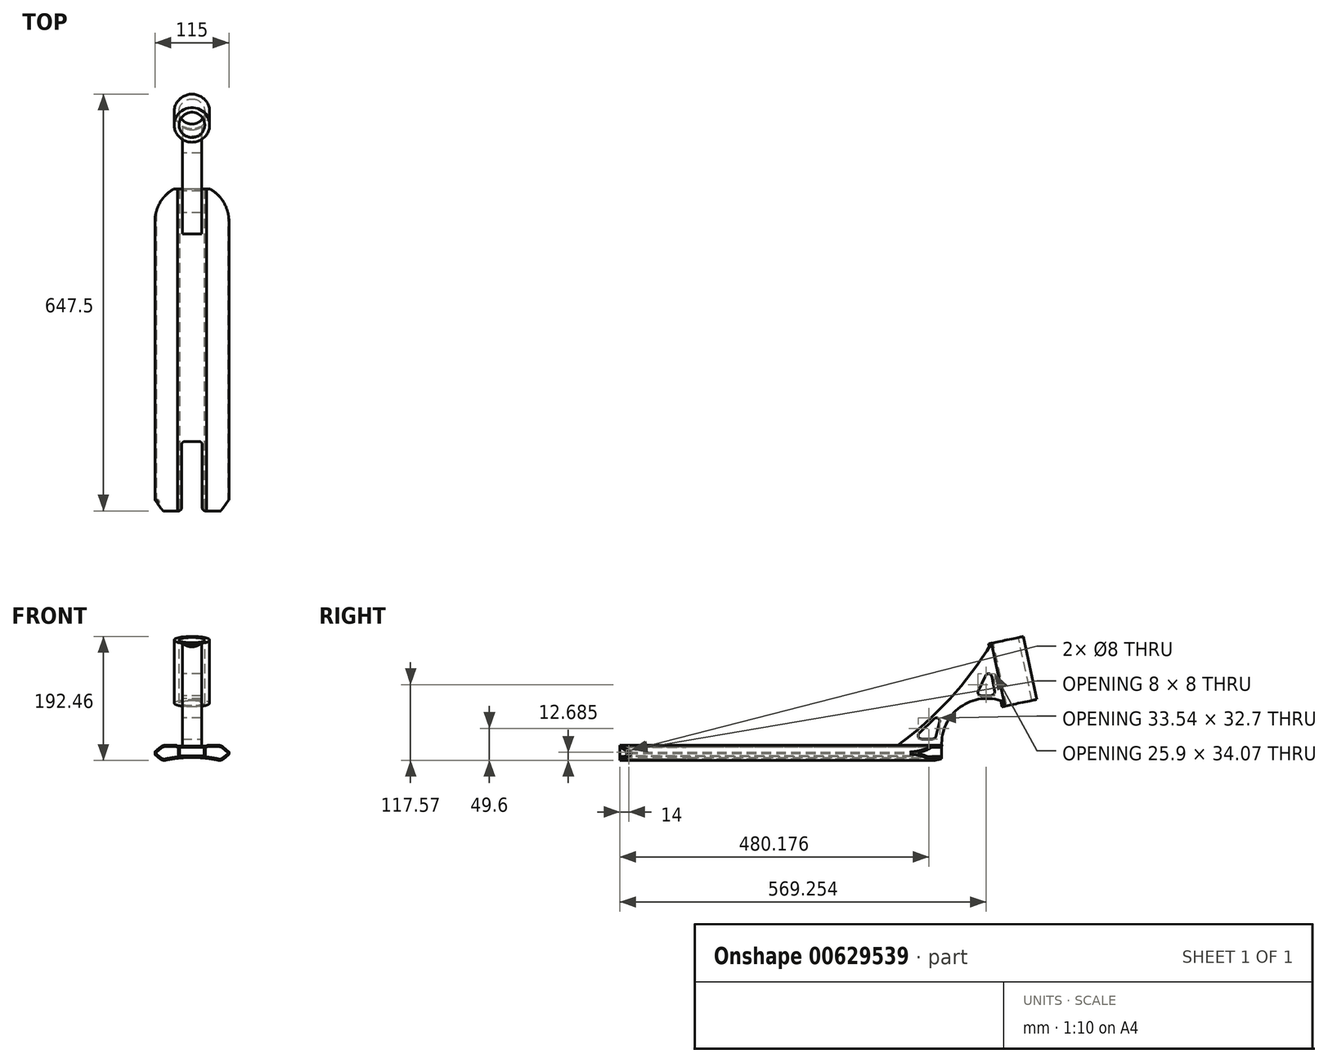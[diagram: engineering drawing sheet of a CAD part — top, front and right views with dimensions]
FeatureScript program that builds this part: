
annotation { "Feature Type Name" : "Feature", "Feature Type Description" : "" }
export const myFeature = defineFeature(function(context is Context, id is Id, definition is map)
    precondition{}
    {
        {
            var Q0;
            Q0=qCreatedBy(makeId("Front.planeOp"),FACE);
            var sketch = newSketch(context, id + "F0", { "sketchPlane" : qUnion([Q0])});
            skLineSegment(sketch, "E0", {"start": v(0, 0) * mm, "end": v(0, 44.87) * mm, "construction": true});
            skLineSegment(sketch, "E1", {"start": v(0, 0) * mm, "end": v(22.5, 0) * mm});
            skLineSegment(sketch, "E2", {"start": v(22.5, 0) * mm, "end": v(22.5, 1.3) * mm});
            skLineSegment(sketch, "E3", {"start": v(22.5, 1.3) * mm, "end": v(45.58, 1.3) * mm});
            skLineSegment(sketch, "E4", {"start": v(45.58, 1.3) * mm, "end": v(57.5, -8.7) * mm});
            skLineSegment(sketch, "E5", {"start": v(57.5, -8.7) * mm, "end": v(57.5, -12.7) * mm});
            skLineSegment(sketch, "E6", {"start": v(57.5, -12.7) * mm, "end": v(45.58, -22.7) * mm});
            skLineSegment(sketch, "E7.MirrorCS", {"start": v(0, 0) * mm, "end": v(-22.5, 0) * mm});
            skLineSegment(sketch, "E8.MirrorCS", {"start": v(-22.5, 0) * mm, "end": v(-22.5, 1.3) * mm});
            skLineSegment(sketch, "E9.MirrorCS", {"start": v(-22.5, 1.3) * mm, "end": v(-45.58, 1.3) * mm});
            skLineSegment(sketch, "E10.MirrorCS", {"start": v(-45.58, 1.3) * mm, "end": v(-57.5, -8.7) * mm});
            skLineSegment(sketch, "E11.MirrorCS", {"start": v(-57.5, -8.7) * mm, "end": v(-57.5, -12.7) * mm});
            skLineSegment(sketch, "E12.MirrorCS", {"start": v(-57.5, -12.7) * mm, "end": v(-45.58, -22.7) * mm});
            skArc(sketch, "E13", {"start": v(45.58, -22.7) * mm, "mid": v(0, -17.44) * mm, "end": v(-45.58, -22.7) * mm});
            skLineSegment(sketch, "E14", {"start": v(-45.58, 1.3) * mm, "end": v(-80.6, 1.3) * mm, "construction": true});
            skLineSegment(sketch, "E15", {"start": v(-57.5, -12.7) * mm, "end": v(-57.5, -34.53) * mm, "construction": true});
            skSolve(sketch);
        }
        {
            var Q0;
            Q0 = qSketchRegion(id + "F0", true);
            extrude(context, id + "F1", {"entities" : qUnion([Q0]), "endBound" : BoundingType.SYMMETRIC, "depth" : 500 * mm, "offsetDistance" : 25 * mm});
        }
        {
            var Q0;
            Q0=makeQuery(id+"F1.opExtrude","CAP_FACE",FACE,{"disambiguationData":[OSD([sQuery(id+"F0.wireOp",EDGE,"E1"),sQuery(id+"F0.wireOp",EDGE,"E2"),sQuery(id+"F0.wireOp",EDGE,"E3"),sQuery(id+"F0.wireOp",EDGE,"E4"),sQuery(id+"F0.wireOp",EDGE,"E5"),sQuery(id+"F0.wireOp",EDGE,"E6"),sQuery(id+"F0.wireOp",EDGE,"E7.MirrorCS"),sQuery(id+"F0.wireOp",EDGE,"E8.MirrorCS"),sQuery(id+"F0.wireOp",EDGE,"E9.MirrorCS"),sQuery(id+"F0.wireOp",EDGE,"E10.MirrorCS"),sQuery(id+"F0.wireOp",EDGE,"E11.MirrorCS"),sQuery(id+"F0.wireOp",EDGE,"E12.MirrorCS"),sQuery(id+"F0.wireOp",EDGE,"E13")])],"isStart":false});
            var sketch = newSketch(context, id + "F2", { "sketchPlane" : qUnion([Q0])});
            skLineSegment(sketch, "E16.bottom", {"start": v(-19, -2) * mm, "end": v(19, -2) * mm});
            skLineSegment(sketch, "E16.top", {"start": v(-19, -15) * mm, "end": v(19, -15) * mm});
            skLineSegment(sketch, "E16.left", {"start": v(-19, -2) * mm, "end": v(-19, -15) * mm});
            skLineSegment(sketch, "E16.right", {"start": v(19, -2) * mm, "end": v(19, -15) * mm});
            skSolve(sketch);
        }
        {
            var Q0;
            Q0 = qSketchRegion(id + "F2", true);
            extrude(context, id + "F3", {"entities" : qUnion([Q0]), "operationType" : NewBodyOperationType.REMOVE, "endBound" : BoundingType.THROUGH_ALL, "oppositeDirection" : true, "depth" : 1068 * mm, "offsetDistance" : 25 * mm});
        }
        {
            var Q0;
            Q0=makeQuery(id+"F1.opExtrude","SWEPT_EDGE",EDGE,{"disambiguationData":[OSD([sQuery(id+"F0.wireOp",EDGE,"E8.MirrorCS"),sQuery(id+"F0.wireOp",EDGE,"E9.MirrorCS")])]});
            var Q1;
            Q1=makeQuery(id+"F1.opExtrude","SWEPT_EDGE",EDGE,{"disambiguationData":[OSD([sQuery(id+"F0.wireOp",EDGE,"E2"),sQuery(id+"F0.wireOp",EDGE,"E3")])]});
            fillet(context, id + "F4", {"entities" : qUnion([Q0, Q1]), "radius" : 2 * mm, "tangentPropagation" : true, "allowEdgeOverflow" : false});
        }
        {
            var Q0;
            Q0=makeQuery(id+"F1.opExtrude","SWEPT_EDGE",EDGE,{"disambiguationData":[OSD([sQuery(id+"F0.wireOp",EDGE,"E9.MirrorCS"),sQuery(id+"F0.wireOp",EDGE,"E10.MirrorCS")])]});
            var Q1;
            Q1=makeQuery(id+"F1.opExtrude","SWEPT_EDGE",EDGE,{"disambiguationData":[OSD([sQuery(id+"F0.wireOp",EDGE,"E3"),sQuery(id+"F0.wireOp",EDGE,"E4")])]});
            var Q2;
            Q2=makeQuery(id+"F1.opExtrude","SWEPT_EDGE",EDGE,{"disambiguationData":[OSD([sQuery(id+"F0.wireOp",EDGE,"E6"),sQuery(id+"F0.wireOp",EDGE,"E13")])]});
            var Q3;
            Q3=makeQuery(id+"F1.opExtrude","SWEPT_EDGE",EDGE,{"disambiguationData":[OSD([sQuery(id+"F0.wireOp",EDGE,"E12.MirrorCS"),sQuery(id+"F0.wireOp",EDGE,"E13")])]});
            fillet(context, id + "F5", {"entities" : qUnion([Q0, Q1, Q2, Q3]), "radius" : 9 * mm, "tangentPropagation" : true, "allowEdgeOverflow" : false});
        }
        {
            var Q0;
            Q0=makeQuery(id+"F1.opExtrude","SWEPT_EDGE",EDGE,{"disambiguationData":[OSD([sQuery(id+"F0.wireOp",EDGE,"E4"),sQuery(id+"F0.wireOp",EDGE,"E5")])]});
            var Q1;
            Q1=makeQuery(id+"F1.opExtrude","SWEPT_EDGE",EDGE,{"disambiguationData":[OSD([sQuery(id+"F0.wireOp",EDGE,"E5"),sQuery(id+"F0.wireOp",EDGE,"E6")])]});
            var Q2;
            Q2=makeQuery(id+"F1.opExtrude","SWEPT_EDGE",EDGE,{"disambiguationData":[OSD([sQuery(id+"F0.wireOp",EDGE,"E10.MirrorCS"),sQuery(id+"F0.wireOp",EDGE,"E11.MirrorCS")])]});
            var Q3;
            Q3=makeQuery(id+"F1.opExtrude","SWEPT_EDGE",EDGE,{"disambiguationData":[OSD([sQuery(id+"F0.wireOp",EDGE,"E11.MirrorCS"),sQuery(id+"F0.wireOp",EDGE,"E12.MirrorCS")])]});
            fillet(context, id + "F6", {"entities" : qUnion([Q0, Q1, Q2, Q3]), "radius" : 1 * mm, "tangentPropagation" : true, "allowEdgeOverflow" : false});
        }
        {
            var Q0;
            Q0=makeQuery(id+"F1.opExtrude","CAP_FACE",FACE,{"disambiguationData":[OSD([sQuery(id+"F0.wireOp",EDGE,"E1"),sQuery(id+"F0.wireOp",EDGE,"E2"),sQuery(id+"F0.wireOp",EDGE,"E3"),sQuery(id+"F0.wireOp",EDGE,"E4"),sQuery(id+"F0.wireOp",EDGE,"E5"),sQuery(id+"F0.wireOp",EDGE,"E6"),sQuery(id+"F0.wireOp",EDGE,"E7.MirrorCS"),sQuery(id+"F0.wireOp",EDGE,"E8.MirrorCS"),sQuery(id+"F0.wireOp",EDGE,"E9.MirrorCS"),sQuery(id+"F0.wireOp",EDGE,"E10.MirrorCS"),sQuery(id+"F0.wireOp",EDGE,"E11.MirrorCS"),sQuery(id+"F0.wireOp",EDGE,"E12.MirrorCS"),sQuery(id+"F0.wireOp",EDGE,"E13")])],"isStart":false});
            var sketch = newSketch(context, id + "F7", { "sketchPlane" : qUnion([Q0])});
            skArc(sketch, "E17.0", {"start": v(-21, -16.53) * mm, "mid": v(-31.42, -17.9) * mm, "end": v(-41.75, -19.8) * mm});
            skArc(sketch, "E17.1", {"start": v(-47.7, -18.31) * mm, "mid": v(-44.9, -19.74) * mm, "end": v(-41.75, -19.8) * mm});
            skLineSegment(sketch, "E17.2", {"start": v(-55.5, -11.77) * mm, "end": v(-47.7, -18.31) * mm});
            skLineSegment(sketch, "E17.3", {"start": v(-55.5, -9.63) * mm, "end": v(-55.5, -11.77) * mm});
            skLineSegment(sketch, "E17.4", {"start": v(-24.37, -0.7) * mm, "end": v(-24.37, -0.7) * mm});
            skLineSegment(sketch, "E17.5", {"start": v(-24.37, -0.7) * mm, "end": v(-42.3, -0.7) * mm});
            skArc(sketch, "E17.6", {"start": v(-42.3, -0.7) * mm, "mid": v(-44.7, -1.12) * mm, "end": v(-46.8, -2.34) * mm});
            skLineSegment(sketch, "E17.7", {"start": v(-46.8, -2.34) * mm, "end": v(-55.5, -9.63) * mm});
            skLineSegment(sketch, "E18", {"start": v(-21, -16.53) * mm, "end": v(-21, -2) * mm});
            skLineSegment(sketch, "E19", {"start": v(-21, -2) * mm, "end": v(-22.88, -2) * mm});
            skArc(sketch, "E20", {"start": v(-22.88, -2) * mm, "mid": v(-23.38, -1.07) * mm, "end": v(-24.37, -0.7) * mm});
            skLineSegment(sketch, "E21.MirrorCS", {"start": v(21, -16.53) * mm, "end": v(21, -2) * mm});
            skLineSegment(sketch, "E22.MirrorCS", {"start": v(21, -2) * mm, "end": v(22.88, -2) * mm});
            skArc(sketch, "E23.MirrorCS", {"start": v(22.88, -2) * mm, "mid": v(23.38, -1.07) * mm, "end": v(24.37, -0.7) * mm});
            skLineSegment(sketch, "E24.MirrorCS", {"start": v(24.37, -0.7) * mm, "end": v(42.3, -0.7) * mm});
            skArc(sketch, "E25.MirrorCS", {"start": v(42.3, -0.7) * mm, "mid": v(44.7, -1.12) * mm, "end": v(46.8, -2.34) * mm});
            skLineSegment(sketch, "E26.MirrorCS", {"start": v(46.8, -2.34) * mm, "end": v(55.5, -9.63) * mm});
            skLineSegment(sketch, "E27.MirrorCS", {"start": v(55.5, -9.63) * mm, "end": v(55.5, -11.77) * mm});
            skLineSegment(sketch, "E28.MirrorCS", {"start": v(55.5, -11.77) * mm, "end": v(47.7, -18.31) * mm});
            skArc(sketch, "E29.MirrorCS", {"start": v(47.7, -18.31) * mm, "mid": v(44.9, -19.74) * mm, "end": v(41.75, -19.8) * mm});
            skArc(sketch, "E30.MirrorCS", {"start": v(21, -16.53) * mm, "mid": v(31.42, -17.9) * mm, "end": v(41.75, -19.8) * mm});
            skSolve(sketch);
        }
        {
            var Q0;
            Q0 = qSketchRegion(id + "F7", true);
            extrude(context, id + "F8", {"entities" : qUnion([Q0]), "operationType" : NewBodyOperationType.REMOVE, "endBound" : BoundingType.THROUGH_ALL, "oppositeDirection" : true, "depth" : 25 * mm, "offsetDistance" : 25 * mm});
        }
        {
            var Q0;
            Q0=qCreatedBy(makeId("Top.planeOp"),FACE);
            var sketch = newSketch(context, id + "F9", { "sketchPlane" : qUnion([Q0])});
            skArc(sketch, "E31", {"start": v(57.5, 200) * mm, "mid": v(0, 257.5) * mm, "end": v(-57.5, 200) * mm});
            skLineSegment(sketch, "E32", {"start": v(-57.5, 200) * mm, "end": v(-57.5, 280) * mm});
            skLineSegment(sketch, "E33", {"start": v(57.5, 200) * mm, "end": v(57.5, 280) * mm});
            skLineSegment(sketch, "E34", {"start": v(57.5, 280) * mm, "end": v(-57.5, 280) * mm});
            skSolve(sketch);
        }
        {
            var Q0;
            Q0 = qSketchRegion(id + "F9", true);
            extrude(context, id + "F10", {"entities" : qUnion([Q0]), "operationType" : NewBodyOperationType.REMOVE, "endBound" : BoundingType.THROUGH_ALL, "oppositeDirection" : true, "depth" : 33 * mm, "offsetDistance" : 25 * mm, "hasSecondDirection" : true, "secondDirectionBound" : SecondDirectionBoundingType.THROUGH_ALL, "secondDirectionOppositeDirection" : false, "secondDirectionDepth" : 25 * mm});
        }
        {
            var Q0;
            Q0=qCreatedBy(makeId("Top.planeOp"),FACE);
            var sketch = newSketch(context, id + "F11", { "sketchPlane" : qUnion([Q0])});
            skLineSegment(sketch, "E35", {"start": v(-16, -252.14) * mm, "end": v(-16, -142.14) * mm});
            skLineSegment(sketch, "E36", {"start": v(-16, -142.14) * mm, "end": v(16, -142.14) * mm});
            skLineSegment(sketch, "E37", {"start": v(16, -142.14) * mm, "end": v(16, -252.14) * mm});
            skLineSegment(sketch, "E38", {"start": v(16, -252.14) * mm, "end": v(43.3, -252.14) * mm});
            skLineSegment(sketch, "E39", {"start": v(43.3, -252.14) * mm, "end": v(68, -218.14) * mm});
            skLineSegment(sketch, "E40", {"start": v(68, -218.14) * mm, "end": v(68, -325.64) * mm});
            skLineSegment(sketch, "E41", {"start": v(68, -325.64) * mm, "end": v(-68, -325.64) * mm});
            skLineSegment(sketch, "E42", {"start": v(-68, -325.64) * mm, "end": v(-68, -218.14) * mm});
            skLineSegment(sketch, "E43", {"start": v(-68, -218.14) * mm, "end": v(-43.3, -252.14) * mm});
            skLineSegment(sketch, "E44", {"start": v(-43.3, -252.14) * mm, "end": v(-16, -252.14) * mm});
            skLineSegment(sketch, "E45", {"start": v(0, 0) * mm, "end": v(0, -350.61) * mm});
            skSolve(sketch);
        }
        {
            var Q0;
            Q0 = qSketchRegion(id + "F11", true);
            extrude(context, id + "F12", {"entities" : qUnion([Q0]), "operationType" : NewBodyOperationType.REMOVE, "endBound" : BoundingType.THROUGH_ALL, "oppositeDirection" : true, "depth" : 25 * mm, "offsetDistance" : 25 * mm, "hasSecondDirection" : true, "secondDirectionBound" : SecondDirectionBoundingType.THROUGH_ALL, "secondDirectionOppositeDirection" : false, "secondDirectionDepth" : 25 * mm});
        }
        {
            var Q0;
            Q0=makeQuery(id+"F12.boolean.opBoolean","INTERSECT",EDGE,{"disambiguationData":[OD(0.0)],"derivedFrom":[makeQuery(id+"F1.opExtrude","CAP_FACE",FACE,{"disambiguationData":[OSD([sQuery(id+"F0.wireOp",EDGE,"E1"),sQuery(id+"F0.wireOp",EDGE,"E2"),sQuery(id+"F0.wireOp",EDGE,"E3"),sQuery(id+"F0.wireOp",EDGE,"E4"),sQuery(id+"F0.wireOp",EDGE,"E5"),sQuery(id+"F0.wireOp",EDGE,"E6"),sQuery(id+"F0.wireOp",EDGE,"E7.MirrorCS"),sQuery(id+"F0.wireOp",EDGE,"E8.MirrorCS"),sQuery(id+"F0.wireOp",EDGE,"E9.MirrorCS"),sQuery(id+"F0.wireOp",EDGE,"E10.MirrorCS"),sQuery(id+"F0.wireOp",EDGE,"E11.MirrorCS"),sQuery(id+"F0.wireOp",EDGE,"E12.MirrorCS"),sQuery(id+"F0.wireOp",EDGE,"E13")])],"isStart":false}),makeQuery(id+"F12.opExtrude","SWEPT_FACE",FACE,{"disambiguationData":[OSD([sQuery(id+"F11.wireOp",EDGE,"E35")])]})]});
            var Q1;
            Q1=makeQuery(id+"F12.boolean.opBoolean","INTERSECT",EDGE,{"disambiguationData":[OD(0.0)],"derivedFrom":[makeQuery(id+"F1.opExtrude","CAP_FACE",FACE,{"disambiguationData":[OSD([sQuery(id+"F0.wireOp",EDGE,"E1"),sQuery(id+"F0.wireOp",EDGE,"E2"),sQuery(id+"F0.wireOp",EDGE,"E3"),sQuery(id+"F0.wireOp",EDGE,"E4"),sQuery(id+"F0.wireOp",EDGE,"E5"),sQuery(id+"F0.wireOp",EDGE,"E6"),sQuery(id+"F0.wireOp",EDGE,"E7.MirrorCS"),sQuery(id+"F0.wireOp",EDGE,"E8.MirrorCS"),sQuery(id+"F0.wireOp",EDGE,"E9.MirrorCS"),sQuery(id+"F0.wireOp",EDGE,"E10.MirrorCS"),sQuery(id+"F0.wireOp",EDGE,"E11.MirrorCS"),sQuery(id+"F0.wireOp",EDGE,"E12.MirrorCS"),sQuery(id+"F0.wireOp",EDGE,"E13")])],"isStart":false}),makeQuery(id+"F12.opExtrude","SWEPT_FACE",FACE,{"disambiguationData":[OSD([sQuery(id+"F11.wireOp",EDGE,"E37")])]})]});
            var Q2;
            {var subQ0=sQuery(id+"F11.wireOp",EDGE,"E35");var subQ1=sQuery(id+"F11.wireOp",EDGE,"E36");Q2=makeQuery(id+"F12.boolean.opBoolean","COPY",EDGE,{"disambiguationData":[TD([makeQuery(id+"F1.opExtrude","SWEPT_FACE",FACE,{"disambiguationData":[OSD([sQuery(id+"F0.wireOp",EDGE,"E13")])]})])],"derivedFrom":makeQuery(id+"F12.opExtrude","SWEPT_EDGE",EDGE,{"disambiguationData":[OSD([subQ0,subQ1])]})});}
            var Q3;
            {var subQ0=sQuery(id+"F11.wireOp",EDGE,"E36");var subQ1=sQuery(id+"F11.wireOp",EDGE,"E37");Q3=makeQuery(id+"F12.boolean.opBoolean","COPY",EDGE,{"disambiguationData":[TD([makeQuery(id+"F1.opExtrude","SWEPT_FACE",FACE,{"disambiguationData":[OSD([sQuery(id+"F0.wireOp",EDGE,"E13")])]})])],"derivedFrom":makeQuery(id+"F12.opExtrude","SWEPT_EDGE",EDGE,{"disambiguationData":[OSD([subQ0,subQ1])]})});}
            var Q4;
            {var subQ0=sQuery(id+"F11.wireOp",EDGE,"E37");var subQ1=sQuery(id+"F11.wireOp",EDGE,"E36");Q4=makeQuery(id+"F12.boolean.opBoolean","COPY",EDGE,{"disambiguationData":[TD([makeQuery(id+"F3.boolean.opBoolean","COPY",FACE,{"derivedFrom":makeQuery(id+"F3.opExtrude","SWEPT_FACE",FACE,{"disambiguationData":[OSD([sQuery(id+"F2.wireOp",EDGE,"E16.bottom")])]})})])],"derivedFrom":makeQuery(id+"F12.opExtrude","SWEPT_EDGE",EDGE,{"disambiguationData":[OSD([subQ1,subQ0])]})});}
            var Q5;
            {var subQ0=sQuery(id+"F11.wireOp",EDGE,"E35");var subQ1=sQuery(id+"F11.wireOp",EDGE,"E36");Q5=makeQuery(id+"F12.boolean.opBoolean","COPY",EDGE,{"disambiguationData":[TD([makeQuery(id+"F3.boolean.opBoolean","COPY",FACE,{"derivedFrom":makeQuery(id+"F3.opExtrude","SWEPT_FACE",FACE,{"disambiguationData":[OSD([sQuery(id+"F2.wireOp",EDGE,"E16.bottom")])]})})])],"derivedFrom":makeQuery(id+"F12.opExtrude","SWEPT_EDGE",EDGE,{"disambiguationData":[OSD([subQ0,subQ1])]})});}
            fillet(context, id + "F13", {"entities" : qUnion([Q0, Q1, Q2, Q3, Q4, Q5]), "radius" : 5 * mm, "tangentPropagation" : true, "allowEdgeOverflow" : false});
        }
        {
            var Q0;
            Q0=qCreatedBy(makeId("Right.planeOp"),FACE);
            var sketch = newSketch(context, id + "F14", { "sketchPlane" : qUnion([Q0])});
            skLineSegment(sketch, "E46", {"start": v(250.12, 0) * mm, "end": v(180.12, 0) * mm});
            skArc(sketch, "E47", {"start": v(180.12, 0) * mm, "mid": v(261.68, 72.66) * mm, "end": v(327.28, 160) * mm});
            skArc(sketch, "E48", {"start": v(345.88, 69.2) * mm, "mid": v(279, 60.9) * mm, "end": v(250.12, 0) * mm});
            skLineSegment(sketch, "E49", {"start": v(327.28, 160) * mm, "end": v(372.28, 169.58) * mm});
            skLineSegment(sketch, "E50", {"start": v(372.28, 169.58) * mm, "end": v(393.1, 71.77) * mm});
            skLineSegment(sketch, "E51", {"start": v(393.1, 71.77) * mm, "end": v(348.1, 62.2) * mm});
            skLineSegment(sketch, "E52", {"start": v(348.1, 62.2) * mm, "end": v(345.88, 69.2) * mm});
            skSolve(sketch);
        }
        {
            var Q0;
            Q0 = qSketchRegion(id + "F14", true);
            extrude(context, id + "F15", {"entities" : qUnion([Q0]), "operationType" : NewBodyOperationType.ADD, "endBound" : BoundingType.SYMMETRIC, "depth" : 30 * mm, "offsetDistance" : 25 * mm});
        }
        {
            var Q0;
            Q0=makeQuery(id+"F15.opExtrude","SWEPT_FACE",FACE,{"disambiguationData":[OSD([sQuery(id+"F14.wireOp",EDGE,"E49")])]});
            var sketch = newSketch(context, id + "F16", { "sketchPlane" : qUnion([Q0])});
            skCircle(sketch, "E53", {"center": v(0, 376.42) * mm, "radius": 27.5 * mm});
            skPoint(sketch, "E53.centerSnap0", {"position": v(15, 376.42) * mm});
            skSolve(sketch);
        }
        {
            var Q0;
            Q0 = qSketchRegion(id + "F16", true);
            var Q1;
            Q1=makeQuery(id+"F15.opExtrude","SWEPT_FACE",FACE,{"disambiguationData":[OSD([sQuery(id+"F14.wireOp",EDGE,"E51")])]});
            extrude(context, id + "F17", {"entities" : qUnion([Q0]), "operationType" : NewBodyOperationType.ADD, "endBound" : BoundingType.UP_TO_SURFACE, "oppositeDirection" : true, "depth" : 25 * mm, "endBoundEntityFace" : qUnion([Q1]), "offsetDistance" : 25 * mm});
        }
        {
            var Q0;
            Q0=makeQuery(id+"F17.boolean.opBoolean","MERGE",FACE,{"derivedFrom":[makeQuery(id+"F15.opExtrude","SWEPT_FACE",FACE,{"disambiguationData":[OSD([sQuery(id+"F14.wireOp",EDGE,"E49")])]}),makeQuery(id+"F17.opExtrude","CAP_FACE",FACE,{"disambiguationData":[OSD([sQuery(id+"F16.wireOp",EDGE,"E53")])],"isStart":true})]});
            var sketch = newSketch(context, id + "F18", { "sketchPlane" : qUnion([Q0])});
            skPoint(sketch, "E54", {"position": v(0, 376.42) * mm});
            skSolve(sketch);
        }
        {
            var Q0;
            Q0=sQuery(id+"F18.wireOp",VERTEX,"E54");
            var Q1;
            Q1=makeQuery(id+"F1.opExtrude","SWEPT_BODY",BODY,{"disambiguationData":[OSD([sQuery(id+"F0.wireOp",EDGE,"E1"),sQuery(id+"F0.wireOp",EDGE,"E2"),sQuery(id+"F0.wireOp",EDGE,"E3"),sQuery(id+"F0.wireOp",EDGE,"E4"),sQuery(id+"F0.wireOp",EDGE,"E5"),sQuery(id+"F0.wireOp",EDGE,"E6"),sQuery(id+"F0.wireOp",EDGE,"E7.MirrorCS"),sQuery(id+"F0.wireOp",EDGE,"E8.MirrorCS"),sQuery(id+"F0.wireOp",EDGE,"E9.MirrorCS"),sQuery(id+"F0.wireOp",EDGE,"E10.MirrorCS"),sQuery(id+"F0.wireOp",EDGE,"E11.MirrorCS"),sQuery(id+"F0.wireOp",EDGE,"E12.MirrorCS"),sQuery(id+"F0.wireOp",EDGE,"E13")])]});
            hole(context, id + "F19", {"style" : HoleStyle.SIMPLE, "endStyle" : HoleEndStyle.THROUGH, "holeDiameter" : 40 * mm, "majorDiameter" : 5 * mm, "isTappedThrough" : true, "tappedDepth" : 12 * mm, "tapClearance" : 3, "locations" : qUnion([Q0]), "scope" : qUnion([Q1])});
        }
        {
            var Q0;
            Q0=makeQuery(id+"F8.boolean.opBoolean","COPY",FACE,{"derivedFrom":makeQuery(id+"F8.opExtrude","SWEPT_FACE",FACE,{"disambiguationData":[OSD([sQuery(id+"F7.wireOp",EDGE,"E21.MirrorCS")])]})});
            var sketch = newSketch(context, id + "F20", { "sketchPlane" : qUnion([Q0])});
            skPoint(sketch, "E55", {"position": v(-236, -9.27) * mm});
            skPoint(sketch, "E55.positionSnap0", {"position": v(-250, -9.27) * mm});
            skSolve(sketch);
        }
        {
            var Q0;
            Q0=sQuery(id+"F20.wireOp",VERTEX,"E55");
            var Q1;
            Q1=makeQuery(id+"F1.opExtrude","SWEPT_BODY",BODY,{"disambiguationData":[OSD([sQuery(id+"F0.wireOp",EDGE,"E1"),sQuery(id+"F0.wireOp",EDGE,"E2"),sQuery(id+"F0.wireOp",EDGE,"E3"),sQuery(id+"F0.wireOp",EDGE,"E4"),sQuery(id+"F0.wireOp",EDGE,"E5"),sQuery(id+"F0.wireOp",EDGE,"E6"),sQuery(id+"F0.wireOp",EDGE,"E7.MirrorCS"),sQuery(id+"F0.wireOp",EDGE,"E8.MirrorCS"),sQuery(id+"F0.wireOp",EDGE,"E9.MirrorCS"),sQuery(id+"F0.wireOp",EDGE,"E10.MirrorCS"),sQuery(id+"F0.wireOp",EDGE,"E11.MirrorCS"),sQuery(id+"F0.wireOp",EDGE,"E12.MirrorCS"),sQuery(id+"F0.wireOp",EDGE,"E13")])]});
            hole(context, id + "F21", {"style" : HoleStyle.SIMPLE, "endStyle" : HoleEndStyle.THROUGH, "holeDiameter" : 8 * mm, "majorDiameter" : 5 * mm, "isTappedThrough" : true, "tappedDepth" : 12 * mm, "tapClearance" : 3, "locations" : qUnion([Q0]), "scope" : qUnion([Q1])});
        }
        {
            var Q0;
            Q0=makeQuery(id+"F15.opExtrude","CAP_FACE",FACE,{"disambiguationData":[OSD([sQuery(id+"F14.wireOp",EDGE,"E46"),sQuery(id+"F14.wireOp",EDGE,"E47"),sQuery(id+"F14.wireOp",EDGE,"E48"),sQuery(id+"F14.wireOp",EDGE,"E49"),sQuery(id+"F14.wireOp",EDGE,"E50"),sQuery(id+"F14.wireOp",EDGE,"E51"),sQuery(id+"F14.wireOp",EDGE,"E52")])],"isStart":false});
            var sketch = newSketch(context, id + "F22", { "sketchPlane" : qUnion([Q0])});
            skLineSegment(sketch, "E56", {"start": v(206, 11.3) * mm, "end": v(240, 11.3) * mm});
            skLineSegment(sketch, "E57", {"start": v(240, 11.3) * mm, "end": v(251.2, 54.89) * mm});
            skLineSegment(sketch, "E58", {"start": v(251.2, 54.89) * mm, "end": v(206, 11.3) * mm});
            skLineSegment(sketch, "E59", {"start": v(303.23, 78.25) * mm, "end": v(333.2, 79.47) * mm});
            skLineSegment(sketch, "E60", {"start": v(333.2, 79.47) * mm, "end": v(324.74, 123.67) * mm});
            skLineSegment(sketch, "E61", {"start": v(324.74, 123.67) * mm, "end": v(303.23, 78.25) * mm});
            skSolve(sketch);
        }
        {
            var Q0;
            Q0 = qSketchRegion(id + "F22", true);
            extrude(context, id + "F23", {"entities" : qUnion([Q0]), "operationType" : NewBodyOperationType.REMOVE, "endBound" : BoundingType.THROUGH_ALL, "oppositeDirection" : true, "depth" : 25 * mm, "offsetDistance" : 25 * mm});
        }
        {
            var Q0;
            Q0=makeQuery(id+"F23.boolean.opBoolean","COPY",EDGE,{"derivedFrom":makeQuery(id+"F23.opExtrude","SWEPT_EDGE",EDGE,{"disambiguationData":[OSD([sQuery(id+"F22.wireOp",EDGE,"E56"),sQuery(id+"F22.wireOp",EDGE,"E58")])]})});
            var Q1;
            Q1=makeQuery(id+"F23.boolean.opBoolean","COPY",EDGE,{"derivedFrom":makeQuery(id+"F23.opExtrude","SWEPT_EDGE",EDGE,{"disambiguationData":[OSD([sQuery(id+"F22.wireOp",EDGE,"E56"),sQuery(id+"F22.wireOp",EDGE,"E57")])]})});
            var Q2;
            Q2=makeQuery(id+"F23.boolean.opBoolean","COPY",EDGE,{"derivedFrom":makeQuery(id+"F23.opExtrude","SWEPT_EDGE",EDGE,{"disambiguationData":[OSD([sQuery(id+"F22.wireOp",EDGE,"E57"),sQuery(id+"F22.wireOp",EDGE,"E58")])]})});
            var Q3;
            Q3=makeQuery(id+"F23.boolean.opBoolean","COPY",EDGE,{"derivedFrom":makeQuery(id+"F23.opExtrude","SWEPT_EDGE",EDGE,{"disambiguationData":[OSD([sQuery(id+"F22.wireOp",EDGE,"E60"),sQuery(id+"F22.wireOp",EDGE,"E61")])]})});
            var Q4;
            Q4=makeQuery(id+"F23.boolean.opBoolean","COPY",EDGE,{"derivedFrom":makeQuery(id+"F23.opExtrude","SWEPT_EDGE",EDGE,{"disambiguationData":[OSD([sQuery(id+"F22.wireOp",EDGE,"E59"),sQuery(id+"F22.wireOp",EDGE,"E61")])]})});
            var Q5;
            Q5=makeQuery(id+"F23.boolean.opBoolean","COPY",EDGE,{"derivedFrom":makeQuery(id+"F23.opExtrude","SWEPT_EDGE",EDGE,{"disambiguationData":[OSD([sQuery(id+"F22.wireOp",EDGE,"E59"),sQuery(id+"F22.wireOp",EDGE,"E60")])]})});
            fillet(context, id + "F24", {"entities" : qUnion([Q0, Q1, Q2, Q3, Q4, Q5]), "radius" : 5 * mm, "tangentPropagation" : true, "allowEdgeOverflow" : false});
        }
    });
